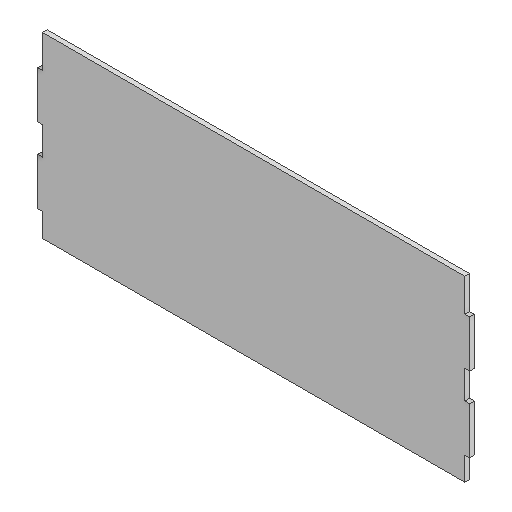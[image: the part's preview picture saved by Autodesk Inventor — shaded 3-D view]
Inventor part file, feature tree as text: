
AUTODESK INVENTOR PART (.ipt)
format: ipt  version: 2022 (Build 260153000, 153)  size: 118,272 bytes
history: native  units: mm
features: reference x8, other x6, extrude x1, sketch x1
ambient origin geometry x8: Origin, YZ Plane, XZ Plane, XY Plane, X Axis, Y Axis, Z Axis, Center Point
bodies: Solid1 (feature_tree)
feature tree (16):
  extrude  "Extrusion1"  Depth=5.0mm
  sketch  "Sketch1"  dims[d0=5.0mm d1=0.0mm d2=5.0mm d3=5.0mm]
  reference  "Reference1"
  reference  "Reference2"
  reference  "Reference3"
  reference  "Reference4"
  reference  "Reference5"
  reference  "Reference6"
  reference  "Reference7"
  reference  "Reference8"
  parser-record x1  (decoder bookkeeping rows leaked as tree rows — omitted from the tree; the rows remain in map.json)
  other  "Ensamble caja.iam"
  other  "Lateral:2"
  other  "Lateral:1"
  other  "Frontal:1"
  other  "Fondo:1"
note: 1 file-system path scrubbed to <path> (originals preserved in map.json)
